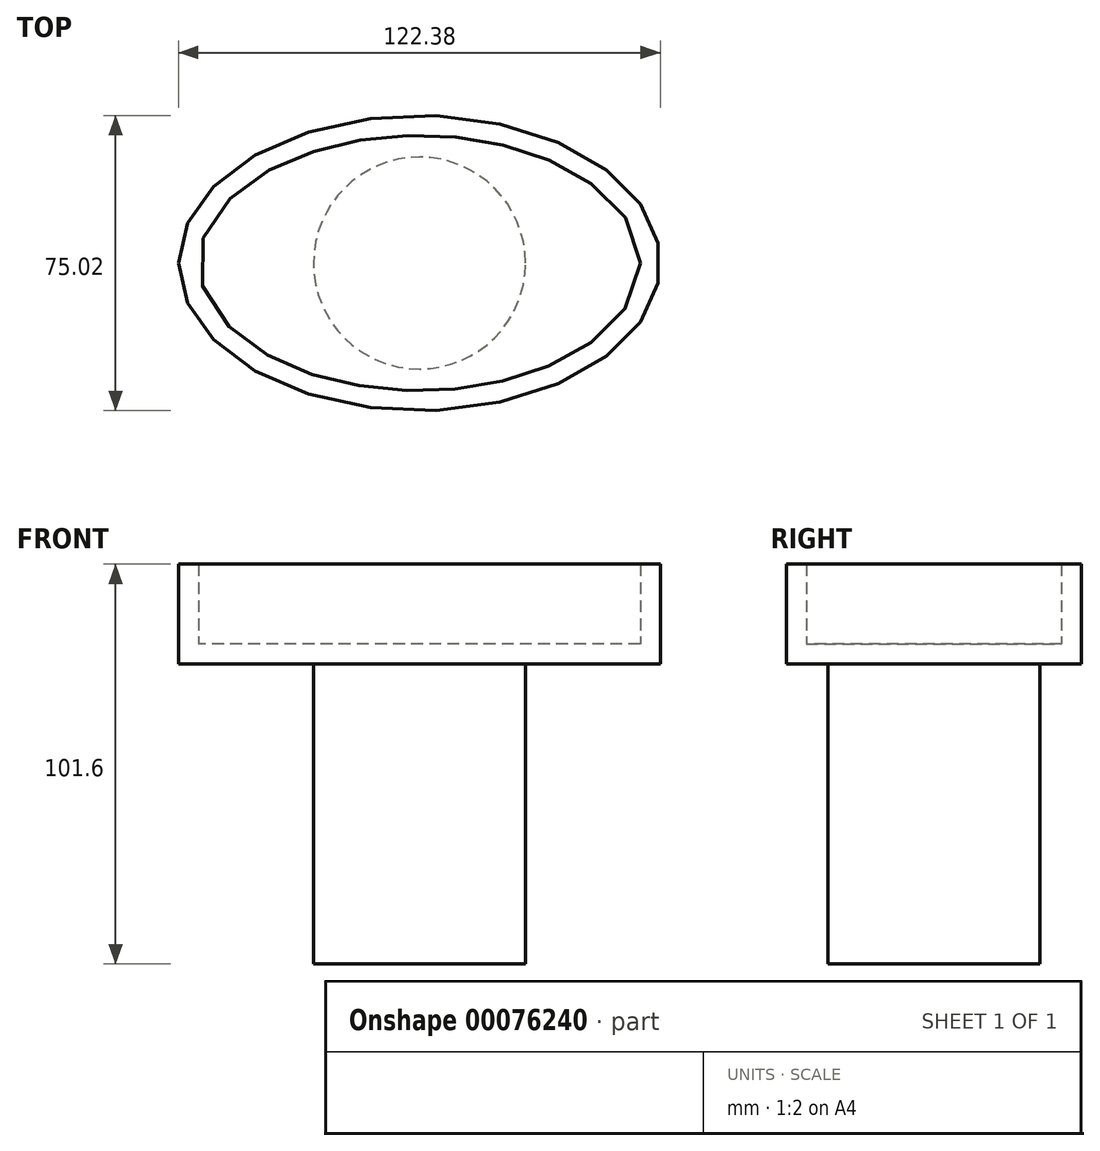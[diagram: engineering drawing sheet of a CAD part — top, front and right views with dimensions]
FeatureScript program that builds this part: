
annotation { "Feature Type Name" : "Feature", "Feature Type Description" : "" }
export const myFeature = defineFeature(function(context is Context, id is Id, definition is map)
    precondition{}
    {
        {
            var Q0;
            Q0=qCreatedBy(makeId("Top.planeOp"),FACE);
            var sketch = newSketch(context, id + "F0", { "sketchPlane" : qUnion([Q0])});
            skEllipse(sketch, "E0", {"center": v(0, 0) * mm, "majorRadius": 61.19 * mm, "minorRadius": 37.51 * mm, "majorAxis": v(-1, 0)});
            skSolve(sketch);
        }
        {
            var Q0;
            Q0=makeQuery(id+"F0.imprint","IMPRINT",FACE,{"disambiguationData":[TD([[makeQuery(id+"F0.imprint","IMPRINT",EDGE,{"derivedFrom":sQuery(id+"F0.wireOp",EDGE,"E0")}),1.0]])]});
            extrude(context, id + "F1", {"entities" : qUnion([Q0]), "depth" : 25.4 * mm});
        }
        {
            var Q0;
            Q0=makeQuery(id+"F1.opExtrude","CAP_FACE",FACE,{"disambiguationData":[OSD([sQuery(id+"F0.wireOp",EDGE,"E0")])],"isStart":false});
            shell(context, id + "F2", {"entities" : qUnion([Q0]), "thickness" : 5.08 * mm});
        }
        {
            var Q0;
            Q0=makeQuery(id+"F1.opExtrude","CAP_FACE",FACE,{"disambiguationData":[OSD([sQuery(id+"F0.wireOp",EDGE,"E0")])],"isStart":true});
            var sketch = newSketch(context, id + "F3", { "sketchPlane" : qUnion([Q0])});
            skCircle(sketch, "E1", {"center": v(0, 0) * mm, "radius": 26.92 * mm});
            skSolve(sketch);
        }
        {
            var Q0;
            Q0=makeQuery(id+"F3.imprint","IMPRINT",FACE,{"disambiguationData":[TD([[makeQuery(id+"F3.imprint","IMPRINT",EDGE,{"derivedFrom":sQuery(id+"F3.wireOp",EDGE,"E1")}),1.0]])]});
            extrude(context, id + "F4", {"entities" : qUnion([Q0]), "operationType" : NewBodyOperationType.ADD, "depth" : 25.4 * mm});
        }
        {
            var Q0;
            Q0=makeQuery(id+"F4.opExtrude","CAP_FACE",FACE,{"disambiguationData":[OSD([sQuery(id+"F3.wireOp",EDGE,"E1")])],"isStart":false});
            extrude(context, id + "F5", {"entities" : qUnion([Q0]), "operationType" : NewBodyOperationType.ADD, "depth" : 50.8 * mm});
        }
    });
